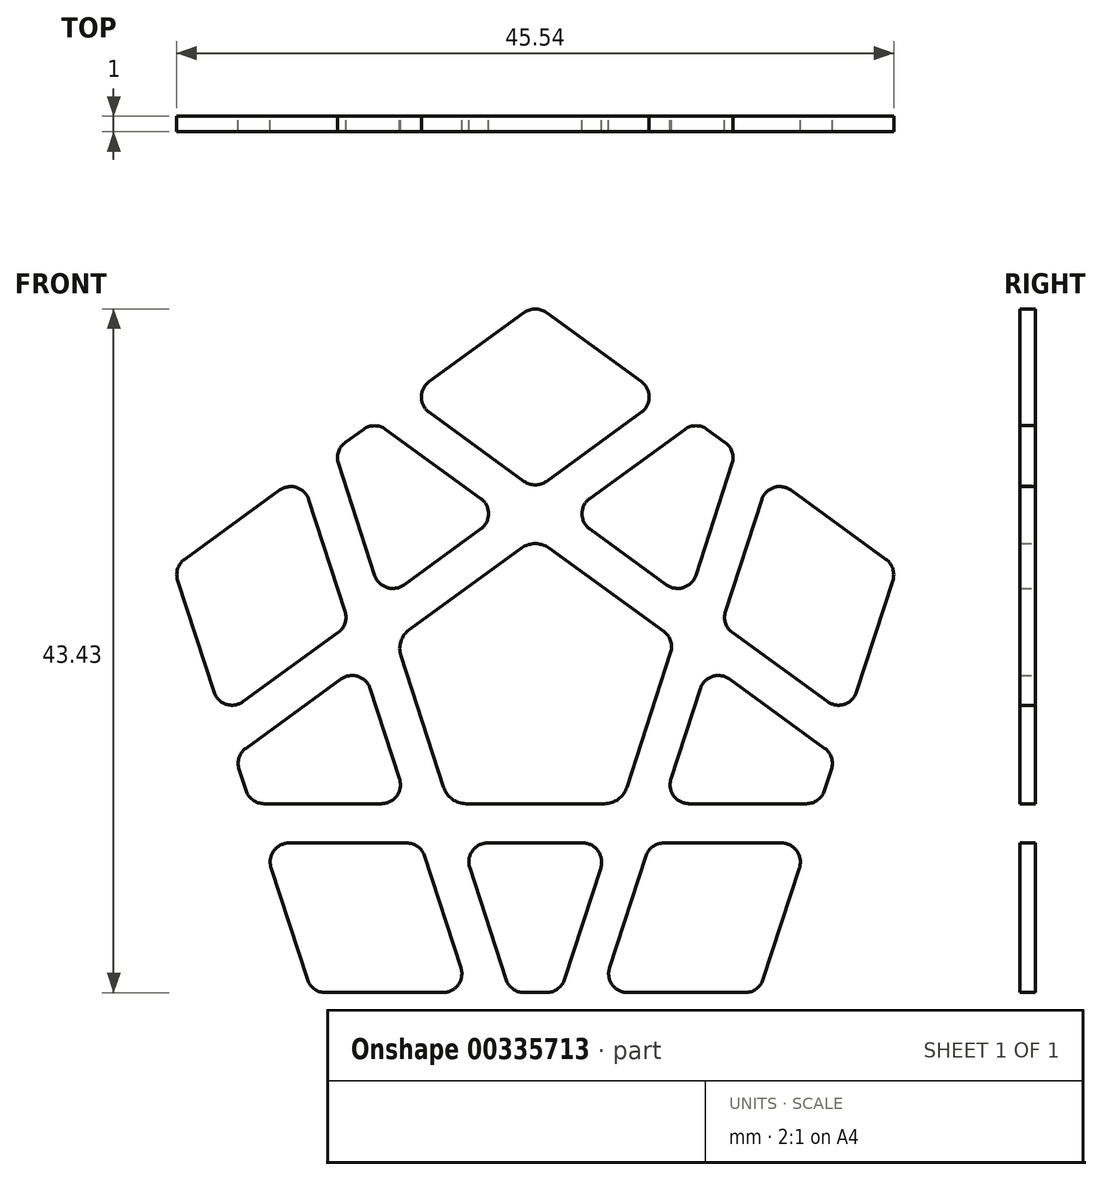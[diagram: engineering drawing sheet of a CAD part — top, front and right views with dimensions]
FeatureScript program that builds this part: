
annotation { "Feature Type Name" : "Feature", "Feature Type Description" : "" }
export const myFeature = defineFeature(function(context is Context, id is Id, definition is map)
    precondition{}
    {
        {
            var Q0;
            Q0=qCreatedBy(makeId("Front.planeOp"),FACE);
            var sketch = newSketch(context, id + "F0", { "sketchPlane" : qUnion([Q0])});
            skCircle(sketch, "E0.cCircle", {"center": v(0, 0) * mm, "radius": 20.8 * mm, "construction": true});
            skLineSegment(sketch, "E0.0", {"start": v(0, 25.7) * mm, "end": v(24.45, 7.94) * mm});
            skLineSegment(sketch, "E0.1", {"start": v(24.45, 7.94) * mm, "end": v(15.1, -20.8) * mm});
            skLineSegment(sketch, "E0.2", {"start": v(15.1, -20.8) * mm, "end": v(-15.1, -20.8) * mm});
            skLineSegment(sketch, "E0.3", {"start": v(-15.1, -20.8) * mm, "end": v(-24.45, 7.94) * mm});
            skLineSegment(sketch, "E0.4", {"start": v(-24.45, 7.94) * mm, "end": v(0, 25.7) * mm});
            skPoint(sketch, "E0.0.midPoint", {"position": v(12.22, 16.82) * mm});
            skLineSegment(sketch, "E1", {"start": v(-19, -8.8) * mm, "end": v(19, -8.8) * mm});
            skLineSegment(sketch, "E2.1.0", {"start": v(2.5, -20.8) * mm, "end": v(14.24, 15.36) * mm});
            skLineSegment(sketch, "E2.2.0", {"start": v(20.55, -4.06) * mm, "end": v(-10.2, 18.29) * mm});
            skLineSegment(sketch, "E2.3.0", {"start": v(10.2, 18.29) * mm, "end": v(-20.55, -4.06) * mm});
            skLineSegment(sketch, "E2.4.0", {"start": v(-14.24, 15.36) * mm, "end": v(-2.5, -20.8) * mm});
            skLineSegment(sketch, "E3", {"start": v(-13.33, -19.55) * mm, "end": v(-5.86, -19.55) * mm});
            skLineSegment(sketch, "E4", {"start": v(-4.72, -17.97) * mm, "end": v(-7.03, -10.87) * mm});
            skLineSegment(sketch, "E5", {"start": v(-8.17, -10.05) * mm, "end": v(-15.64, -10.05) * mm});
            skLineSegment(sketch, "E6", {"start": v(-16.78, -11.62) * mm, "end": v(-14.47, -18.72) * mm});
            skPoint(sketch, "E7.visualSharp", {"position": v(-17.29, -10.05) * mm});
            skArc(sketch, "E7.filletArc", {"start": v(-15.64, -10.05) * mm, "mid": v(-16.6, -10.54) * mm, "end": v(-16.78, -11.62) * mm});
            skPoint(sketch, "E8.visualSharp", {"position": v(-7.3, -10.05) * mm});
            skArc(sketch, "E8.filletArc", {"start": v(-7.03, -10.87) * mm, "mid": v(-7.46, -10.27) * mm, "end": v(-8.17, -10.05) * mm});
            skPoint(sketch, "E9.visualSharp", {"position": v(-4.21, -19.55) * mm});
            skArc(sketch, "E9.filletArc", {"start": v(-5.86, -19.55) * mm, "mid": v(-4.9, -19.05) * mm, "end": v(-4.72, -17.97) * mm});
            skPoint(sketch, "E10.visualSharp", {"position": v(-14.2, -19.55) * mm});
            skArc(sketch, "E10.filletArc", {"start": v(-14.47, -18.72) * mm, "mid": v(-14.03, -19.32) * mm, "end": v(-13.33, -19.55) * mm});
            skLineSegment(sketch, "E11", {"start": v(-3.02, -10.05) * mm, "end": v(3.02, -10.05) * mm});
            skLineSegment(sketch, "E12", {"start": v(4.16, -11.62) * mm, "end": v(1.85, -18.72) * mm});
            skLineSegment(sketch, "E13", {"start": v(0.71, -19.55) * mm, "end": v(-0.71, -19.55) * mm});
            skLineSegment(sketch, "E14", {"start": v(-1.85, -18.72) * mm, "end": v(-4.16, -11.62) * mm});
            skPoint(sketch, "E15.visualSharp", {"position": v(-1.58, -19.55) * mm});
            skArc(sketch, "E15.filletArc", {"start": v(-1.85, -18.72) * mm, "mid": v(-1.42, -19.32) * mm, "end": v(-0.71, -19.55) * mm});
            skPoint(sketch, "E16.visualSharp", {"position": v(1.58, -19.55) * mm});
            skArc(sketch, "E16.filletArc", {"start": v(0.71, -19.55) * mm, "mid": v(1.42, -19.32) * mm, "end": v(1.85, -18.72) * mm});
            skPoint(sketch, "E17.visualSharp", {"position": v(4.67, -10.05) * mm});
            skArc(sketch, "E17.filletArc", {"start": v(4.16, -11.62) * mm, "mid": v(3.99, -10.54) * mm, "end": v(3.02, -10.05) * mm});
            skPoint(sketch, "E18.visualSharp", {"position": v(-4.67, -10.05) * mm});
            skArc(sketch, "E18.filletArc", {"start": v(-3.02, -10.05) * mm, "mid": v(-3.99, -10.54) * mm, "end": v(-4.16, -11.62) * mm});
            skLineSegment(sketch, "E19.1.0", {"start": v(7.03, -10.87) * mm, "end": v(4.72, -17.97) * mm});
            skArc(sketch, "E19.1.1", {"start": v(4.72, -17.97) * mm, "mid": v(4.9, -19.05) * mm, "end": v(5.86, -19.55) * mm});
            skLineSegment(sketch, "E19.1.2", {"start": v(5.86, -19.55) * mm, "end": v(13.33, -19.55) * mm});
            skArc(sketch, "E19.1.3", {"start": v(13.33, -19.55) * mm, "mid": v(14.03, -19.32) * mm, "end": v(14.47, -18.72) * mm});
            skLineSegment(sketch, "E19.1.4", {"start": v(14.47, -18.72) * mm, "end": v(16.78, -11.62) * mm});
            skArc(sketch, "E19.1.5", {"start": v(16.78, -11.62) * mm, "mid": v(16.6, -10.54) * mm, "end": v(15.64, -10.05) * mm});
            skLineSegment(sketch, "E19.1.6", {"start": v(15.64, -10.05) * mm, "end": v(8.17, -10.05) * mm});
            skArc(sketch, "E19.1.7", {"start": v(8.17, -10.05) * mm, "mid": v(7.46, -10.27) * mm, "end": v(7.03, -10.87) * mm});
            skArc(sketch, "E19.1.8", {"start": v(8.62, -5.97) * mm, "mid": v(8.8, -7.05) * mm, "end": v(9.76, -7.55) * mm});
            skLineSegment(sketch, "E19.1.9", {"start": v(8.62, -5.97) * mm, "end": v(10.49, -0.23) * mm});
            skArc(sketch, "E19.1.10", {"start": v(12.33, 0.37) * mm, "mid": v(11.26, 0.54) * mm, "end": v(10.49, -0.23) * mm});
            skLineSegment(sketch, "E19.1.11", {"start": v(12.33, 0.37) * mm, "end": v(18.37, -4.02) * mm});
            skArc(sketch, "E19.1.12", {"start": v(18.8, -5.36) * mm, "mid": v(18.8, -4.62) * mm, "end": v(18.37, -4.02) * mm});
            skLineSegment(sketch, "E19.1.13", {"start": v(18.8, -5.36) * mm, "end": v(18.37, -6.72) * mm});
            skArc(sketch, "E19.1.14", {"start": v(17.23, -7.55) * mm, "mid": v(17.93, -7.32) * mm, "end": v(18.37, -6.72) * mm});
            skLineSegment(sketch, "E19.1.15", {"start": v(17.23, -7.55) * mm, "end": v(9.76, -7.55) * mm});
            skLineSegment(sketch, "E19.2.0", {"start": v(12.51, 3.32) * mm, "end": v(18.55, -1.06) * mm});
            skArc(sketch, "E19.2.1", {"start": v(18.55, -1.06) * mm, "mid": v(19.63, -1.23) * mm, "end": v(20.4, -0.46) * mm});
            skLineSegment(sketch, "E19.2.2", {"start": v(20.4, -0.46) * mm, "end": v(22.7, 6.64) * mm});
            skArc(sketch, "E19.2.3", {"start": v(22.7, 6.64) * mm, "mid": v(22.7, 7.38) * mm, "end": v(22.27, 7.98) * mm});
            skLineSegment(sketch, "E19.2.4", {"start": v(22.27, 7.98) * mm, "end": v(16.23, 12.37) * mm});
            skArc(sketch, "E19.2.5", {"start": v(16.23, 12.37) * mm, "mid": v(15.16, 12.54) * mm, "end": v(14.39, 11.77) * mm});
            skLineSegment(sketch, "E19.2.6", {"start": v(14.39, 11.77) * mm, "end": v(12.08, 4.67) * mm});
            skArc(sketch, "E19.2.7", {"start": v(12.08, 4.67) * mm, "mid": v(12.08, 3.92) * mm, "end": v(12.51, 3.32) * mm});
            skArc(sketch, "E19.2.8", {"start": v(8.35, 6.35) * mm, "mid": v(9.42, 6.18) * mm, "end": v(10.2, 6.95) * mm});
            skLineSegment(sketch, "E19.2.9", {"start": v(8.35, 6.35) * mm, "end": v(3.46, 9.9) * mm});
            skArc(sketch, "E19.2.10", {"start": v(3.46, 11.84) * mm, "mid": v(2.97, 10.87) * mm, "end": v(3.46, 9.9) * mm});
            skLineSegment(sketch, "E19.2.11", {"start": v(3.46, 11.84) * mm, "end": v(9.5, 16.23) * mm});
            skArc(sketch, "E19.2.12", {"start": v(10.91, 16.23) * mm, "mid": v(10.2, 16.46) * mm, "end": v(9.5, 16.23) * mm});
            skLineSegment(sketch, "E19.2.13", {"start": v(10.91, 16.23) * mm, "end": v(12.06, 15.4) * mm});
            skArc(sketch, "E19.2.14", {"start": v(12.5, 14.05) * mm, "mid": v(12.5, 14.8) * mm, "end": v(12.06, 15.4) * mm});
            skLineSegment(sketch, "E19.2.15", {"start": v(12.5, 14.05) * mm, "end": v(10.2, 6.95) * mm});
            skLineSegment(sketch, "E19.3.0", {"start": v(0.7, 12.93) * mm, "end": v(6.74, 17.32) * mm});
            skArc(sketch, "E19.3.1", {"start": v(6.74, 17.32) * mm, "mid": v(7.24, 18.29) * mm, "end": v(6.74, 19.26) * mm});
            skLineSegment(sketch, "E19.3.2", {"start": v(6.74, 19.26) * mm, "end": v(0.7, 23.65) * mm});
            skArc(sketch, "E19.3.3", {"start": v(0.7, 23.65) * mm, "mid": v(0, 23.88) * mm, "end": v(-0.7, 23.65) * mm});
            skLineSegment(sketch, "E19.3.4", {"start": v(-0.7, 23.65) * mm, "end": v(-6.74, 19.26) * mm});
            skArc(sketch, "E19.3.5", {"start": v(-6.74, 19.26) * mm, "mid": v(-7.24, 18.29) * mm, "end": v(-6.74, 17.32) * mm});
            skLineSegment(sketch, "E19.3.6", {"start": v(-6.74, 17.32) * mm, "end": v(-0.7, 12.93) * mm});
            skArc(sketch, "E19.3.7", {"start": v(-0.7, 12.93) * mm, "mid": v(0, 12.7) * mm, "end": v(0.7, 12.93) * mm});
            skArc(sketch, "E19.3.8", {"start": v(-3.46, 9.9) * mm, "mid": v(-2.97, 10.87) * mm, "end": v(-3.46, 11.84) * mm});
            skLineSegment(sketch, "E19.3.9", {"start": v(-3.46, 9.9) * mm, "end": v(-8.35, 6.35) * mm});
            skArc(sketch, "E19.3.10", {"start": v(-10.2, 6.95) * mm, "mid": v(-9.42, 6.18) * mm, "end": v(-8.35, 6.35) * mm});
            skLineSegment(sketch, "E19.3.11", {"start": v(-10.2, 6.95) * mm, "end": v(-12.5, 14.05) * mm});
            skArc(sketch, "E19.3.12", {"start": v(-12.06, 15.4) * mm, "mid": v(-12.5, 14.8) * mm, "end": v(-12.5, 14.05) * mm});
            skLineSegment(sketch, "E19.3.13", {"start": v(-12.06, 15.4) * mm, "end": v(-10.91, 16.23) * mm});
            skArc(sketch, "E19.3.14", {"start": v(-9.5, 16.23) * mm, "mid": v(-10.2, 16.46) * mm, "end": v(-10.91, 16.23) * mm});
            skLineSegment(sketch, "E19.3.15", {"start": v(-9.5, 16.23) * mm, "end": v(-3.46, 11.84) * mm});
            skLineSegment(sketch, "E19.4.0", {"start": v(-12.08, 4.67) * mm, "end": v(-14.39, 11.77) * mm});
            skArc(sketch, "E19.4.1", {"start": v(-14.39, 11.77) * mm, "mid": v(-15.16, 12.54) * mm, "end": v(-16.23, 12.37) * mm});
            skLineSegment(sketch, "E19.4.2", {"start": v(-16.23, 12.37) * mm, "end": v(-22.27, 7.98) * mm});
            skArc(sketch, "E19.4.3", {"start": v(-22.27, 7.98) * mm, "mid": v(-22.7, 7.38) * mm, "end": v(-22.7, 6.64) * mm});
            skLineSegment(sketch, "E19.4.4", {"start": v(-22.7, 6.64) * mm, "end": v(-20.4, -0.46) * mm});
            skArc(sketch, "E19.4.5", {"start": v(-20.4, -0.46) * mm, "mid": v(-19.63, -1.23) * mm, "end": v(-18.55, -1.06) * mm});
            skLineSegment(sketch, "E19.4.6", {"start": v(-18.55, -1.06) * mm, "end": v(-12.51, 3.32) * mm});
            skArc(sketch, "E19.4.7", {"start": v(-12.51, 3.32) * mm, "mid": v(-12.08, 3.92) * mm, "end": v(-12.08, 4.67) * mm});
            skArc(sketch, "E19.4.8", {"start": v(-10.49, -0.23) * mm, "mid": v(-11.26, 0.54) * mm, "end": v(-12.33, 0.37) * mm});
            skLineSegment(sketch, "E19.4.9", {"start": v(-10.49, -0.23) * mm, "end": v(-8.62, -5.97) * mm});
            skArc(sketch, "E19.4.10", {"start": v(-9.76, -7.55) * mm, "mid": v(-8.8, -7.05) * mm, "end": v(-8.62, -5.97) * mm});
            skLineSegment(sketch, "E19.4.11", {"start": v(-9.76, -7.55) * mm, "end": v(-17.23, -7.55) * mm});
            skArc(sketch, "E19.4.12", {"start": v(-18.37, -6.72) * mm, "mid": v(-17.93, -7.32) * mm, "end": v(-17.23, -7.55) * mm});
            skLineSegment(sketch, "E19.4.13", {"start": v(-18.37, -6.72) * mm, "end": v(-18.8, -5.36) * mm});
            skArc(sketch, "E19.4.14", {"start": v(-18.37, -4.02) * mm, "mid": v(-18.8, -4.62) * mm, "end": v(-18.8, -5.36) * mm});
            skLineSegment(sketch, "E19.4.15", {"start": v(-18.37, -4.02) * mm, "end": v(-12.33, 0.37) * mm});
            skCircle(sketch, "E20.cCircle", {"center": v(0, 0) * mm, "radius": 7.55 * mm, "construction": true});
            skLineSegment(sketch, "E20.0", {"start": v(4.4, -7.55) * mm, "end": v(-4.4, -7.55) * mm});
            skLineSegment(sketch, "E20.1", {"start": v(-5.82, -6.5) * mm, "end": v(-8.53, 1.85) * mm});
            skLineSegment(sketch, "E20.2", {"start": v(-7.99, 3.52) * mm, "end": v(-0.88, 8.69) * mm});
            skLineSegment(sketch, "E20.3", {"start": v(0.88, 8.69) * mm, "end": v(8.16, 3.4) * mm});
            skLineSegment(sketch, "E20.4", {"start": v(8.6, 2.05) * mm, "end": v(5.82, -6.5) * mm});
            skPoint(sketch, "E20.0.midPoint", {"position": v(0, -7.55) * mm});
            skPoint(sketch, "E21.visualSharp", {"position": v(0, 9.33) * mm});
            skArc(sketch, "E21.filletArc", {"start": v(0.88, 8.69) * mm, "mid": v(0, 8.97) * mm, "end": v(-0.88, 8.69) * mm});
            skPoint(sketch, "E22.visualSharp", {"position": v(8.87, 2.88) * mm});
            skArc(sketch, "E22.filletArc", {"start": v(8.6, 2.05) * mm, "mid": v(8.6, 2.8) * mm, "end": v(8.16, 3.4) * mm});
            skPoint(sketch, "E23.visualSharp", {"position": v(5.48, -7.55) * mm});
            skArc(sketch, "E23.filletArc", {"start": v(4.4, -7.55) * mm, "mid": v(5.27, -7.26) * mm, "end": v(5.82, -6.5) * mm});
            skPoint(sketch, "E24.visualSharp", {"position": v(-5.48, -7.55) * mm});
            skArc(sketch, "E24.filletArc", {"start": v(-5.82, -6.5) * mm, "mid": v(-5.27, -7.26) * mm, "end": v(-4.4, -7.55) * mm});
            skPoint(sketch, "E25.visualSharp", {"position": v(-8.87, 2.88) * mm});
            skArc(sketch, "E25.filletArc", {"start": v(-7.99, 3.52) * mm, "mid": v(-8.53, 2.77) * mm, "end": v(-8.53, 1.85) * mm});
            skSolve(sketch);
        }
        {
            var Q0;
            Q0=makeQuery(id+"F0.imprint","IMPRINT",FACE,{"disambiguationData":[TD([[makeQuery(id+"F0.imprint","IMPRINT",EDGE,{"derivedFrom":sQuery(id+"F0.wireOp",EDGE,"E19.4.0")}),1.0]])]});
            var Q1;
            Q1=makeQuery(id+"F0.imprint","IMPRINT",FACE,{"disambiguationData":[TD([[makeQuery(id+"F0.imprint","IMPRINT",EDGE,{"derivedFrom":sQuery(id+"F0.wireOp",EDGE,"E19.3.8")}),1.0]])]});
            var Q2;
            Q2=makeQuery(id+"F0.imprint","IMPRINT",FACE,{"disambiguationData":[TD([[makeQuery(id+"F0.imprint","IMPRINT",EDGE,{"derivedFrom":sQuery(id+"F0.wireOp",EDGE,"E19.3.0")}),1.0]])]});
            var Q3;
            Q3=makeQuery(id+"F0.imprint","IMPRINT",FACE,{"disambiguationData":[TD([[makeQuery(id+"F0.imprint","IMPRINT",EDGE,{"derivedFrom":sQuery(id+"F0.wireOp",EDGE,"E19.2.8")}),1.0]])]});
            var Q4;
            Q4=makeQuery(id+"F0.imprint","IMPRINT",FACE,{"disambiguationData":[TD([[makeQuery(id+"F0.imprint","IMPRINT",EDGE,{"derivedFrom":sQuery(id+"F0.wireOp",EDGE,"E20.0")}),-1.0]])]});
            var Q5;
            Q5=makeQuery(id+"F0.imprint","IMPRINT",FACE,{"disambiguationData":[TD([[makeQuery(id+"F0.imprint","IMPRINT",EDGE,{"derivedFrom":sQuery(id+"F0.wireOp",EDGE,"E19.4.8")}),1.0]])]});
            var Q6;
            Q6=makeQuery(id+"F0.imprint","IMPRINT",FACE,{"disambiguationData":[TD([[makeQuery(id+"F0.imprint","IMPRINT",EDGE,{"derivedFrom":sQuery(id+"F0.wireOp",EDGE,"E3")}),1.0]])]});
            var Q7;
            Q7=makeQuery(id+"F0.imprint","IMPRINT",FACE,{"disambiguationData":[TD([[makeQuery(id+"F0.imprint","IMPRINT",EDGE,{"derivedFrom":sQuery(id+"F0.wireOp",EDGE,"E11")}),-1.0]])]});
            var Q8;
            Q8=makeQuery(id+"F0.imprint","IMPRINT",FACE,{"disambiguationData":[TD([[makeQuery(id+"F0.imprint","IMPRINT",EDGE,{"derivedFrom":sQuery(id+"F0.wireOp",EDGE,"E19.1.0")}),1.0]])]});
            var Q9;
            Q9=makeQuery(id+"F0.imprint","IMPRINT",FACE,{"disambiguationData":[TD([[makeQuery(id+"F0.imprint","IMPRINT",EDGE,{"derivedFrom":sQuery(id+"F0.wireOp",EDGE,"E19.1.8")}),1.0]])]});
            var Q10;
            Q10=makeQuery(id+"F0.imprint","IMPRINT",FACE,{"disambiguationData":[TD([[makeQuery(id+"F0.imprint","IMPRINT",EDGE,{"derivedFrom":sQuery(id+"F0.wireOp",EDGE,"E19.2.0")}),1.0]])]});
            extrude(context, id + "F1", {"entities" : qUnion([Q0, Q1, Q2, Q3, Q4, Q5, Q6, Q7, Q8, Q9, Q10]), "depth" : 1 * mm});
        }
    });
